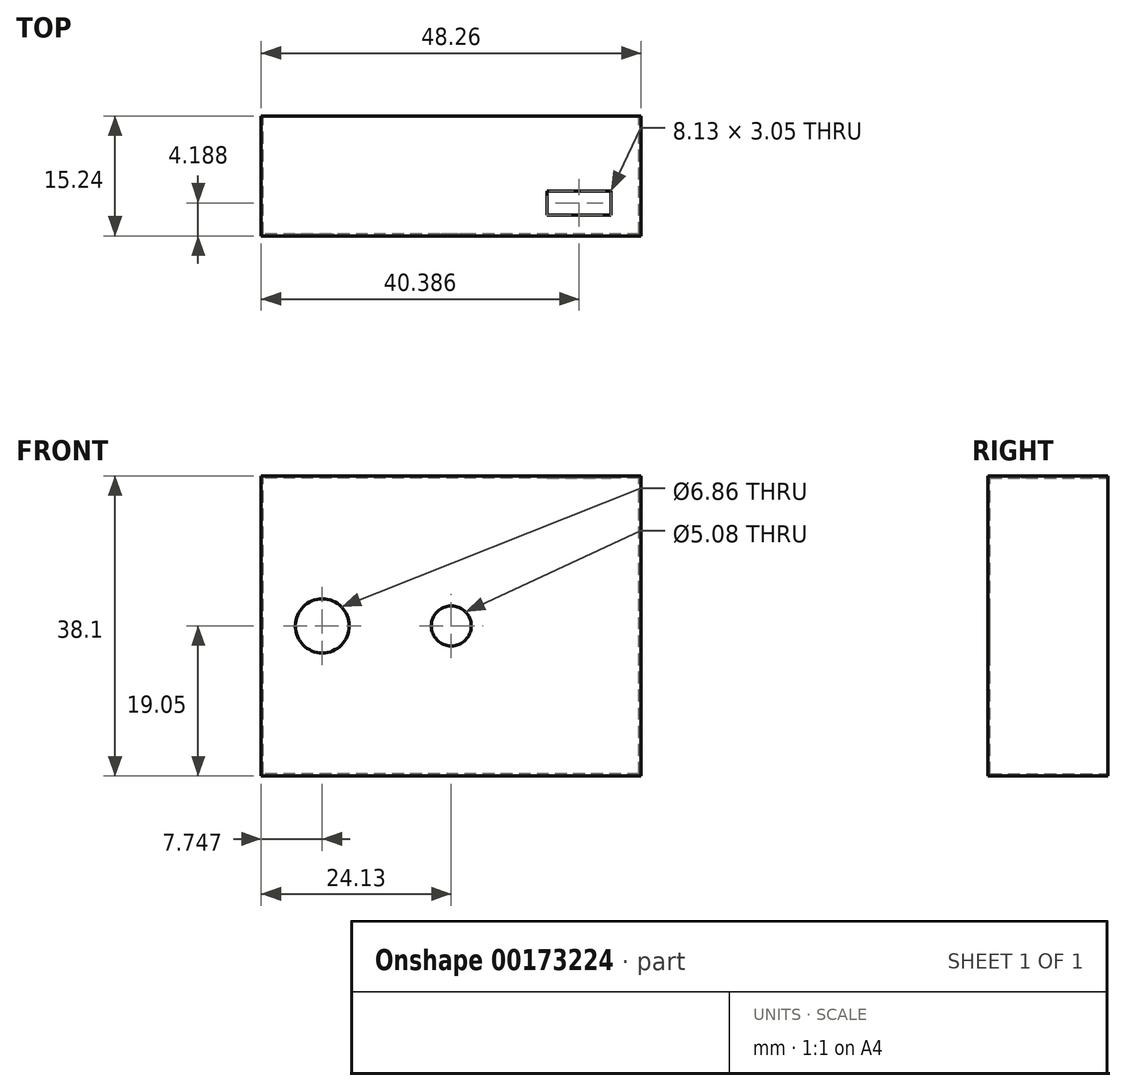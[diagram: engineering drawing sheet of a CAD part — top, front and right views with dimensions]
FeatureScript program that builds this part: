
annotation { "Feature Type Name" : "Feature", "Feature Type Description" : "" }
export const myFeature = defineFeature(function(context is Context, id is Id, definition is map)
    precondition{}
    {
        {
            var Q0;
            Q0=qCreatedBy(makeId("Front.planeOp"),FACE);
            var sketch = newSketch(context, id + "F0", { "sketchPlane" : qUnion([Q0])});
            skLineSegment(sketch, "E0.bottom", {"start": v(24.13, -19.05) * mm, "end": v(-24.13, -19.05) * mm});
            skLineSegment(sketch, "E0.top", {"start": v(24.13, 19.05) * mm, "end": v(-24.13, 19.05) * mm});
            skLineSegment(sketch, "E0.left", {"start": v(24.13, -19.05) * mm, "end": v(24.13, 19.05) * mm});
            skLineSegment(sketch, "E0.right", {"start": v(-24.13, -19.05) * mm, "end": v(-24.13, 19.05) * mm});
            skPoint(sketch, "E0.middle", {"position": v(0, 0) * mm});
            skSolve(sketch);
        }
        {
            var Q0;
            Q0=makeQuery(id+"F0.imprint","IMPRINT",FACE,{"disambiguationData":[TD([[makeQuery(id+"F0.imprint","IMPRINT",EDGE,{"derivedFrom":sQuery(id+"F0.wireOp",EDGE,"E0.bottom")}),-1.0]])]});
            extrude(context, id + "F1", {"entities" : qUnion([Q0]), "depth" : 15.24 * mm});
        }
        {
            var Q0;
            Q0=makeQuery(id+"F1.opExtrude","CAP_FACE",FACE,{"disambiguationData":[OSD([sQuery(id+"F0.wireOp",EDGE,"E0.bottom"),sQuery(id+"F0.wireOp",EDGE,"E0.top"),sQuery(id+"F0.wireOp",EDGE,"E0.left"),sQuery(id+"F0.wireOp",EDGE,"E0.right")])],"isStart":false});
            var sketch = newSketch(context, id + "F2", { "sketchPlane" : qUnion([Q0])});
            skLineSegment(sketch, "E1", {"start": v(-24.13, 2.53) * mm, "end": v(-19.81, 2.53) * mm});
            skLineSegment(sketch, "E2", {"start": v(-24.13, 0) * mm, "end": v(-16.38, 0) * mm});
            skPoint(sketch, "E2.endSnap0", {"position": v(-24.13, 0) * mm});
            skPoint(sketch, "E3.middle", {"position": v(-16.38, 0) * mm});
            skCircle(sketch, "E4", {"center": v(-16.38, 0) * mm, "radius": 3.43 * mm});
            skSolve(sketch);
        }
        {
            var Q0;
            Q0=makeQuery(id+"F1.opExtrude","CAP_FACE",FACE,{"disambiguationData":[OSD([sQuery(id+"F0.wireOp",EDGE,"E0.bottom"),sQuery(id+"F0.wireOp",EDGE,"E0.top"),sQuery(id+"F0.wireOp",EDGE,"E0.left"),sQuery(id+"F0.wireOp",EDGE,"E0.right")])],"isStart":true});
            shell(context, id + "F3", {"entities" : qUnion([Q0]), "thickness" : 0.25 * mm});
        }
        {
            var Q0;
            Q0=sQuery(id+"F2.wireOp",VERTEX,"E3.middle");
            var Q1;
            Q1=makeQuery(id+"F1.opExtrude","SWEPT_BODY",BODY,{"disambiguationData":[OSD([sQuery(id+"F0.wireOp",EDGE,"E0.bottom"),sQuery(id+"F0.wireOp",EDGE,"E0.top"),sQuery(id+"F0.wireOp",EDGE,"E0.left"),sQuery(id+"F0.wireOp",EDGE,"E0.right")])]});
            hole(context, id + "F4", {"style" : HoleStyle.SIMPLE, "endStyle" : HoleEndStyle.THROUGH, "holeDiameter" : 6.86 * mm, "locations" : qUnion([Q0]), "scope" : qUnion([Q1]), "isTappedThrough" : true});
        }
        {
            var Q0;
            Q0=makeQuery(id+"F1.opExtrude","CAP_FACE",FACE,{"disambiguationData":[OSD([sQuery(id+"F0.wireOp",EDGE,"E0.bottom"),sQuery(id+"F0.wireOp",EDGE,"E0.top"),sQuery(id+"F0.wireOp",EDGE,"E0.left"),sQuery(id+"F0.wireOp",EDGE,"E0.right")])],"isStart":false});
            var sketch = newSketch(context, id + "F5", { "sketchPlane" : qUnion([Q0])});
            skCircle(sketch, "E5", {"center": v(0, 0) * mm, "radius": 2.54 * mm});
            skSolve(sketch);
        }
        {
            var Q0;
            Q0=sQuery(id+"F5.wireOp",VERTEX,"E5.center");
            var Q1;
            Q1=makeQuery(id+"F1.opExtrude","SWEPT_BODY",BODY,{"disambiguationData":[OSD([sQuery(id+"F0.wireOp",EDGE,"E0.bottom"),sQuery(id+"F0.wireOp",EDGE,"E0.top"),sQuery(id+"F0.wireOp",EDGE,"E0.left"),sQuery(id+"F0.wireOp",EDGE,"E0.right")])]});
            hole(context, id + "F6", {"style" : HoleStyle.SIMPLE, "endStyle" : HoleEndStyle.THROUGH, "holeDiameter" : 5.08 * mm, "locations" : qUnion([Q0]), "scope" : qUnion([Q1]), "isTappedThrough" : true});
        }
        {
            var Q0;
            Q0=makeQuery(id+"F1.opExtrude","SWEPT_FACE",FACE,{"disambiguationData":[OSD([sQuery(id+"F0.wireOp",EDGE,"E0.top")])]});
            var sketch = newSketch(context, id + "F7", { "sketchPlane" : qUnion([Q0])});
            skLineSegment(sketch, "E6", {"start": v(24.13, -15.24) * mm, "end": v(20.32, -15.24) * mm});
            skLineSegment(sketch, "E7", {"start": v(24.13, -15.24) * mm, "end": v(24.13, -13.2) * mm});
            skLineSegment(sketch, "E8", {"start": v(20.32, -15.24) * mm, "end": v(20.32, -13.2) * mm});
            skLineSegment(sketch, "E9", {"start": v(20.32, -15.24) * mm, "end": v(12.2, -15.24) * mm});
            skLineSegment(sketch, "E10", {"start": v(24.13, -13.2) * mm, "end": v(24.13, -10.16) * mm});
            skLineSegment(sketch, "E11.bottom", {"start": v(20.32, -12.58) * mm, "end": v(12.2, -12.58) * mm});
            skLineSegment(sketch, "E11.top", {"start": v(20.32, -9.53) * mm, "end": v(12.2, -9.53) * mm});
            skLineSegment(sketch, "E11.left", {"start": v(20.32, -12.58) * mm, "end": v(20.32, -9.53) * mm});
            skLineSegment(sketch, "E11.right", {"start": v(12.2, -12.58) * mm, "end": v(12.2, -9.53) * mm});
            skSolve(sketch);
        }
        {
            var Q0;
            Q0=makeQuery(id+"F7.imprint","IMPRINT",FACE,{"disambiguationData":[TD([[makeQuery(id+"F7.imprint","IMPRINT",EDGE,{"derivedFrom":sQuery(id+"F7.wireOp",EDGE,"E11.bottom")}),-1.0]])]});
            extrude(context, id + "F8", {"entities" : qUnion([Q0]), "operationType" : NewBodyOperationType.REMOVE, "oppositeDirection" : true, "depth" : 25.4 * mm});
        }
    });
